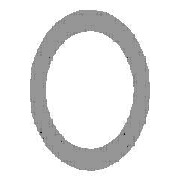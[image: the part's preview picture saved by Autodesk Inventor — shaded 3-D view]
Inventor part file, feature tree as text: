
AUTODESK INVENTOR PART (.ipt)
format: ipt  version: 2013 (Build 170138000, 138)  size: 126,464 bytes
history: native  units: mm (DEFAULTED — no unit token found)
features: plane x7, sketch x5, other x4, extrude x2
ambient origin geometry x8: Origin, YZ Plane, XZ Plane, XY Plane, X Axis, Y Axis, Z Axis, Center Point
bodies: Solid1 (feature_tree), Body (feature_tree)
feature tree (18):
  parser-record x1  (decoder bookkeeping rows leaked as tree rows — omitted from the tree; the rows remain in map.json)
  other  "Driven Length"
  other  "Start plane"
  other  "End plane"
  plane  "Work Plane4"
  plane  "Work Plane5"
  plane  "Work Plane6"
  extrude  "Extrusion2"  Depth=3.556mm
  plane  "Work Plane7"
  plane  "Work Plane8"
  plane  "Work Plane9"
  extrude  "Extrusion3"  TaperAngle=0.0deg  [1 undecoded]
  sketch  "Sketch"  dims[d7=406.4mm d8=3.302mm d9=0.0mm d10=3.302mm d11=0.0mm]
  sketch  "Sketch3"  dims[d0=42.164mm d1=3.556mm]
  plane  "Work Plane3"
  sketch  "Sketch4"  dims[d2=406.4mm d3=0.0mm d4=-0.0mm]
  sketch  "Sketch5"  dims[d5=406.4mm]
  sketch  "Sketch6"  dims[d6=90.0deg]
note: 1 required parameter value undecoded (feature->parameter linkage not recoverable at this tier; creation-order binding heuristic only, values carry confidence <= 0.55)
